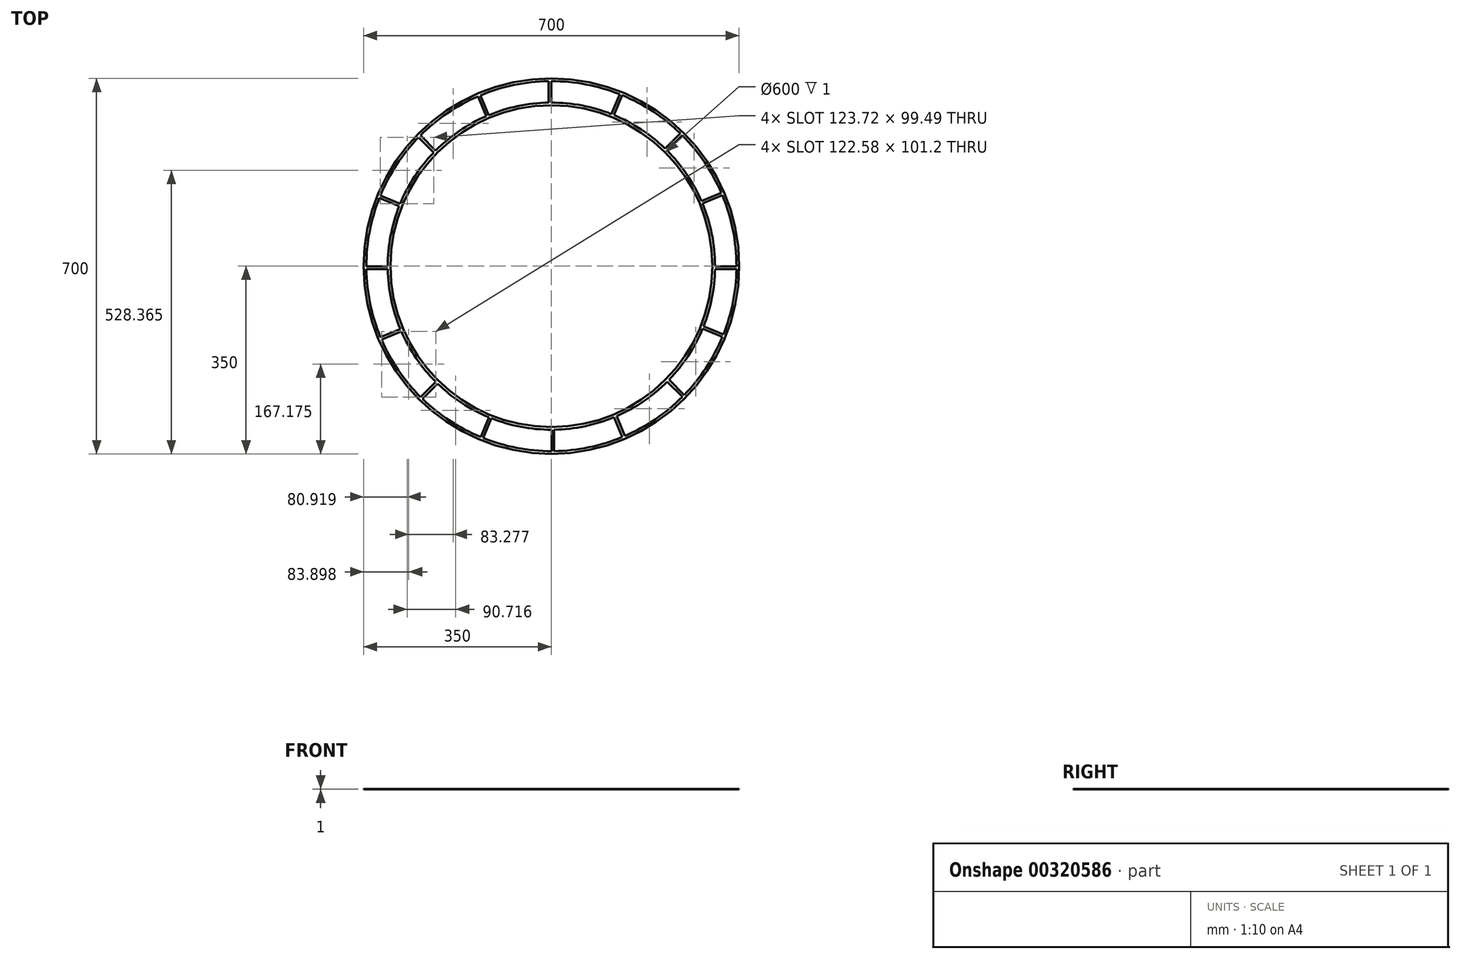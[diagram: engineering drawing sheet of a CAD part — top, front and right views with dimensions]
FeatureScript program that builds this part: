
annotation { "Feature Type Name" : "Feature", "Feature Type Description" : "" }
export const myFeature = defineFeature(function(context is Context, id is Id, definition is map)
    precondition{}
    {
        {
            var Q0;
            Q0=qCreatedBy(makeId("Top.planeOp"),FACE);
            var sketch = newSketch(context, id + "F0", { "sketchPlane" : qUnion([Q0])});
            skCircle(sketch, "E0", {"center": v(0, 0) * mm, "radius": 300 * mm});
            skArc(sketch, "E1", {"start": v(345, -0.2) * mm, "mid": v(338.37, 67.32) * mm, "end": v(318.65, 132.24) * mm});
            skCircle(sketch, "E2", {"center": v(0, 0) * mm, "radius": 350 * mm});
            skArc(sketch, "E3", {"start": v(305, -0.27) * mm, "mid": v(299.14, 59.48) * mm, "end": v(281.7, 116.93) * mm});
            skLineSegment(sketch, "E4", {"start": v(0, 0) * mm, "end": v(528.74, 0) * mm, "construction": true});
            skLineSegment(sketch, "E5.right", {"start": v(288.09, 5.23) * mm, "end": v(288.09, 0) * mm});
            skPoint(sketch, "E5.middle", {"position": v(324.27, 0) * mm});
            skLineSegment(sketch, "E6.1.0", {"start": v(331.02, 142.78) * mm, "end": v(321.32, 138.76) * mm});
            skLineSegment(sketch, "E6.1.1", {"start": v(332.97, 138.17) * mm, "end": v(323.27, 134.15) * mm});
            skLineSegment(sketch, "E6.2.0", {"start": v(251.18, 258.58) * mm, "end": v(243.76, 251.16) * mm});
            skLineSegment(sketch, "E6.2.1", {"start": v(254.75, 255.08) * mm, "end": v(247.32, 247.65) * mm});
            skLineSegment(sketch, "E6.3.0", {"start": v(133.1, 335.02) * mm, "end": v(129.1, 325.32) * mm});
            skLineSegment(sketch, "E6.3.1", {"start": v(137.74, 333.15) * mm, "end": v(133.73, 323.45) * mm});
            skLineSegment(sketch, "E6.4.1", {"start": v(-0.23, 360.5) * mm, "end": v(-0.23, 350) * mm});
            skLineSegment(sketch, "E6.5.0", {"start": v(-142.78, 331.02) * mm, "end": v(-138.76, 321.32) * mm});
            skLineSegment(sketch, "E6.5.1", {"start": v(-138.17, 332.97) * mm, "end": v(-134.15, 323.27) * mm});
            skLineSegment(sketch, "E6.6.0", {"start": v(-258.58, 251.18) * mm, "end": v(-251.16, 243.76) * mm});
            skLineSegment(sketch, "E6.6.1", {"start": v(-255.08, 254.75) * mm, "end": v(-247.65, 247.32) * mm});
            skLineSegment(sketch, "E6.7.0", {"start": v(-335.02, 133.1) * mm, "end": v(-283.74, 111.87) * mm});
            skLineSegment(sketch, "E6.7.1", {"start": v(-333.15, 137.74) * mm, "end": v(-281.87, 116.5) * mm});
            skLineSegment(sketch, "E6.8.0", {"start": v(-360.46, -5.23) * mm, "end": v(-349.96, -5.23) * mm});
            skLineSegment(sketch, "E6.8.1", {"start": v(-360.5, -0.23) * mm, "end": v(-350, -0.23) * mm});
            skLineSegment(sketch, "E6.9.0", {"start": v(-331.02, -142.78) * mm, "end": v(-321.32, -138.76) * mm});
            skLineSegment(sketch, "E6.9.1", {"start": v(-332.97, -138.17) * mm, "end": v(-323.27, -134.15) * mm});
            skLineSegment(sketch, "E6.10.0", {"start": v(-251.18, -258.58) * mm, "end": v(-243.76, -251.16) * mm});
            skLineSegment(sketch, "E6.10.1", {"start": v(-254.75, -255.08) * mm, "end": v(-247.32, -247.65) * mm});
            skLineSegment(sketch, "E6.11.0", {"start": v(-133.1, -335.02) * mm, "end": v(-129.1, -325.32) * mm});
            skLineSegment(sketch, "E6.11.1", {"start": v(-137.74, -333.15) * mm, "end": v(-133.73, -323.45) * mm});
            skLineSegment(sketch, "E6.12.0", {"start": v(5.23, -360.46) * mm, "end": v(5.23, -349.96) * mm});
            skLineSegment(sketch, "E6.12.1", {"start": v(0.23, -360.5) * mm, "end": v(0.23, -350) * mm});
            skLineSegment(sketch, "E6.13.0", {"start": v(142.78, -331.02) * mm, "end": v(138.76, -321.32) * mm});
            skLineSegment(sketch, "E6.13.1", {"start": v(138.17, -332.97) * mm, "end": v(134.15, -323.27) * mm});
            skLineSegment(sketch, "E6.14.0", {"start": v(258.58, -251.18) * mm, "end": v(251.16, -243.76) * mm});
            skLineSegment(sketch, "E6.14.1", {"start": v(255.08, -254.75) * mm, "end": v(247.65, -247.32) * mm});
            skLineSegment(sketch, "E6.15.0", {"start": v(335.02, -133.1) * mm, "end": v(325.32, -129.1) * mm});
            skLineSegment(sketch, "E6.15.1", {"start": v(333.15, -137.74) * mm, "end": v(323.45, -133.73) * mm});
            skPoint(sketch, "E7.orphan", {"position": v(288.09, -5.23) * mm});
            skLineSegment(sketch, "E8.trimOffspring", {"start": v(345, -0.2) * mm, "end": v(305, -0.27) * mm});
            skLineSegment(sketch, "E9.trimOffspring", {"start": v(344.96, -5.2) * mm, "end": v(304.95, -5.27) * mm});
            skPoint(sketch, "E5.left.start.orphan", {"position": v(360.46, 5.23) * mm});
            skPoint(sketch, "E5.top.start.orphan", {"position": v(360.46, -5.23) * mm});
            skArc(sketch, "E10.trimOffspring", {"start": v(316.7, 136.84) * mm, "mid": v(285.33, 193.94) * mm, "end": v(243.79, 244.12) * mm});
            skArc(sketch, "E11.trimOffspring", {"start": v(279.74, 121.53) * mm, "mid": v(252.07, 171.71) * mm, "end": v(215.5, 215.83) * mm});
            skArc(sketch, "E12.trimOffspring", {"start": v(211.94, 219.34) * mm, "mid": v(167.17, 255.1) * mm, "end": v(116.5, 281.87) * mm});
            skArc(sketch, "E13.trimOffspring", {"start": v(240.22, 247.62) * mm, "mid": v(189.4, 288.37) * mm, "end": v(131.81, 318.83) * mm});
            skArc(sketch, "E14.trimOffspring", {"start": v(127.18, 320.7) * mm, "mid": v(64.62, 338.9) * mm, "end": v(-0.23, 345) * mm});
            skArc(sketch, "E15.trimOffspring", {"start": v(111.87, 283.74) * mm, "mid": v(56.82, 299.66) * mm, "end": v(-0.23, 305) * mm});
            skArc(sketch, "E16.trimOffspring", {"start": v(-5.23, 344.96) * mm, "mid": v(-69.98, 337.83) * mm, "end": v(-132.24, 318.65) * mm});
            skArc(sketch, "E17.trimOffspring", {"start": v(-5.23, 304.96) * mm, "mid": v(-62.18, 298.6) * mm, "end": v(-116.93, 281.7) * mm});
            skArc(sketch, "E18.trimOffspring", {"start": v(-136.84, 316.7) * mm, "mid": v(-193.94, 285.33) * mm, "end": v(-244.12, 243.79) * mm});
            skArc(sketch, "E19.trimOffspring", {"start": v(-121.53, 279.74) * mm, "mid": v(-171.71, 252.07) * mm, "end": v(-215.83, 215.5) * mm});
            skArc(sketch, "E20.trimOffspring", {"start": v(-247.62, 240.22) * mm, "mid": v(-288.37, 189.4) * mm, "end": v(-318.83, 131.81) * mm});
            skArc(sketch, "E21.trimOffspring", {"start": v(-219.34, 211.94) * mm, "mid": v(-255.1, 167.17) * mm, "end": v(-281.87, 116.5) * mm});
            skArc(sketch, "E22.trimOffspring", {"start": v(-320.7, 127.18) * mm, "mid": v(-338.9, 64.62) * mm, "end": v(-345, -0.23) * mm});
            skArc(sketch, "E23.trimOffspring", {"start": v(-283.74, 111.87) * mm, "mid": v(-299.66, 56.82) * mm, "end": v(-305, -0.23) * mm});
            skArc(sketch, "E24.trimOffspring", {"start": v(-344.96, -5.23) * mm, "mid": v(-337.83, -69.98) * mm, "end": v(-318.65, -132.24) * mm});
            skArc(sketch, "E25.trimOffspring", {"start": v(-304.96, -5.23) * mm, "mid": v(-298.6, -62.18) * mm, "end": v(-281.7, -116.93) * mm});
            skArc(sketch, "E26.trimOffspring", {"start": v(-279.74, -121.53) * mm, "mid": v(-252.07, -171.71) * mm, "end": v(-215.5, -215.83) * mm});
            skArc(sketch, "E27.trimOffspring", {"start": v(-211.94, -219.34) * mm, "mid": v(-167.17, -255.1) * mm, "end": v(-116.5, -281.87) * mm});
            skArc(sketch, "E28.trimOffspring", {"start": v(-240.22, -247.62) * mm, "mid": v(-189.4, -288.37) * mm, "end": v(-131.81, -318.83) * mm});
            skArc(sketch, "E29.trimOffspring", {"start": v(-111.87, -283.74) * mm, "mid": v(-56.82, -299.66) * mm, "end": v(0.23, -305) * mm});
            skArc(sketch, "E30.trimOffspring", {"start": v(-127.18, -320.7) * mm, "mid": v(-64.62, -338.9) * mm, "end": v(0.23, -345) * mm});
            skArc(sketch, "E31.trimOffspring", {"start": v(5.23, -304.96) * mm, "mid": v(62.18, -298.6) * mm, "end": v(116.93, -281.7) * mm});
            skArc(sketch, "E32.trimOffspring", {"start": v(5.23, -344.96) * mm, "mid": v(69.98, -337.83) * mm, "end": v(132.24, -318.65) * mm});
            skArc(sketch, "E33.trimOffspring", {"start": v(136.84, -316.7) * mm, "mid": v(193.94, -285.33) * mm, "end": v(244.12, -243.79) * mm});
            skArc(sketch, "E34.trimOffspring", {"start": v(121.53, -279.74) * mm, "mid": v(171.71, -252.07) * mm, "end": v(215.83, -215.5) * mm});
            skArc(sketch, "E35.trimOffspring", {"start": v(219.34, -211.94) * mm, "mid": v(255.1, -167.17) * mm, "end": v(281.87, -116.5) * mm});
            skArc(sketch, "E36.trimOffspring", {"start": v(247.62, -240.22) * mm, "mid": v(288.37, -189.4) * mm, "end": v(318.83, -131.81) * mm});
            skArc(sketch, "E37.trimOffspring", {"start": v(283.74, -111.87) * mm, "mid": v(299.14, -59.52) * mm, "end": v(304.95, -5.27) * mm});
            skArc(sketch, "E38.trimOffspring", {"start": v(320.7, -127.18) * mm, "mid": v(338.37, -67.29) * mm, "end": v(344.96, -5.2) * mm});
            skLineSegment(sketch, "E39.trimOffspring", {"start": v(275.12, 119.62) * mm, "end": v(264.16, 115.08) * mm});
            skLineSegment(sketch, "E40.trimOffspring", {"start": v(277.08, 115.02) * mm, "end": v(266.11, 110.48) * mm});
            skLineSegment(sketch, "E41.trimOffspring", {"start": v(316.7, 136.84) * mm, "end": v(279.74, 121.53) * mm});
            skLineSegment(sketch, "E42.trimOffspring", {"start": v(318.65, 132.24) * mm, "end": v(281.7, 116.93) * mm});
            skLineSegment(sketch, "E43.trimOffspring", {"start": v(240.22, 247.62) * mm, "end": v(211.94, 219.34) * mm});
            skLineSegment(sketch, "E44.trimOffspring", {"start": v(243.79, 244.12) * mm, "end": v(215.5, 215.83) * mm});
            skLineSegment(sketch, "E45.trimOffspring", {"start": v(211.97, 212.3) * mm, "end": v(203.58, 203.9) * mm});
            skLineSegment(sketch, "E46.trimOffspring", {"start": v(208.4, 215.8) * mm, "end": v(200.01, 207.4) * mm});
            skLineSegment(sketch, "E47.trimOffspring", {"start": v(127.18, 320.7) * mm, "end": v(111.87, 283.74) * mm});
            skLineSegment(sketch, "E48.trimOffspring", {"start": v(131.81, 318.83) * mm, "end": v(116.5, 281.87) * mm});
            skLineSegment(sketch, "E49.trimOffspring", {"start": v(109.95, 279.12) * mm, "end": v(105.41, 268.16) * mm});
            skLineSegment(sketch, "E50.trimOffspring", {"start": v(114.6, 277.25) * mm, "end": v(110.05, 266.29) * mm});
            skLineSegment(sketch, "E51.trimOffspring", {"start": v(-0.23, 345) * mm, "end": v(-0.23, 305) * mm});
            skLineSegment(sketch, "E52.trimOffspring", {"start": v(-5.23, 344.96) * mm, "end": v(-5.23, 304.96) * mm});
            skLineSegment(sketch, "E53.trimOffspring", {"start": v(-0.23, 300) * mm, "end": v(-0.23, 288.13) * mm});
            skLineSegment(sketch, "E54.trimOffspring", {"start": v(-5.23, 299.95) * mm, "end": v(-5.23, 288.09) * mm});
            skLineSegment(sketch, "E55.trimOffspring", {"start": v(-132.24, 318.65) * mm, "end": v(-116.93, 281.7) * mm});
            skLineSegment(sketch, "E56.trimOffspring", {"start": v(-136.84, 316.7) * mm, "end": v(-121.53, 279.74) * mm});
            skLineSegment(sketch, "E57.trimOffspring", {"start": v(-115.02, 277.08) * mm, "end": v(-110.48, 266.11) * mm});
            skLineSegment(sketch, "E58.trimOffspring", {"start": v(-119.62, 275.12) * mm, "end": v(-115.08, 264.16) * mm});
            skLineSegment(sketch, "E59.trimOffspring", {"start": v(-244.12, 243.79) * mm, "end": v(-215.83, 215.5) * mm});
            skLineSegment(sketch, "E60.trimOffspring", {"start": v(-247.62, 240.22) * mm, "end": v(-219.34, 211.94) * mm});
            skLineSegment(sketch, "E61.trimOffspring", {"start": v(-212.3, 211.97) * mm, "end": v(-203.9, 203.58) * mm});
            skLineSegment(sketch, "E62.trimOffspring", {"start": v(-215.8, 208.4) * mm, "end": v(-207.4, 200.01) * mm});
            skLineSegment(sketch, "E63.trimOffspring", {"start": v(-277.25, 114.6) * mm, "end": v(-266.29, 110.05) * mm});
            skLineSegment(sketch, "E64.trimOffspring", {"start": v(-279.12, 109.95) * mm, "end": v(-268.16, 105.41) * mm});
            skLineSegment(sketch, "E65.trimOffspring", {"start": v(-300, -0.23) * mm, "end": v(-288.13, -0.23) * mm});
            skLineSegment(sketch, "E66.trimOffspring", {"start": v(-299.95, -5.23) * mm, "end": v(-288.09, -5.23) * mm});
            skLineSegment(sketch, "E67.trimOffspring", {"start": v(-344.96, -5.23) * mm, "end": v(-304.96, -5.23) * mm});
            skLineSegment(sketch, "E68.trimOffspring", {"start": v(-345, -0.23) * mm, "end": v(-305, -0.23) * mm});
            skLineSegment(sketch, "E69.trimOffspring", {"start": v(-277.08, -115.02) * mm, "end": v(-266.11, -110.48) * mm});
            skLineSegment(sketch, "E70.trimOffspring", {"start": v(-275.12, -119.62) * mm, "end": v(-264.16, -115.08) * mm});
            skLineSegment(sketch, "E71.trimOffspring", {"start": v(-316.7, -136.84) * mm, "end": v(-279.74, -121.53) * mm});
            skLineSegment(sketch, "E72.trimOffspring", {"start": v(-318.65, -132.24) * mm, "end": v(-281.7, -116.93) * mm});
            skArc(sketch, "E73.trimOffspring", {"start": v(-316.7, -136.84) * mm, "mid": v(-285.33, -193.94) * mm, "end": v(-243.79, -244.12) * mm});
            skLineSegment(sketch, "E74.trimOffspring", {"start": v(-243.79, -244.12) * mm, "end": v(-215.5, -215.83) * mm});
            skLineSegment(sketch, "E75.trimOffspring", {"start": v(-240.22, -247.62) * mm, "end": v(-211.94, -219.34) * mm});
            skLineSegment(sketch, "E76.trimOffspring", {"start": v(-211.97, -212.3) * mm, "end": v(-203.58, -203.9) * mm});
            skLineSegment(sketch, "E77.trimOffspring", {"start": v(-208.4, -215.8) * mm, "end": v(-200.01, -207.4) * mm});
            skLineSegment(sketch, "E78.trimOffspring", {"start": v(-114.6, -277.25) * mm, "end": v(-110.05, -266.29) * mm});
            skLineSegment(sketch, "E79.trimOffspring", {"start": v(-131.81, -318.83) * mm, "end": v(-116.5, -281.87) * mm});
            skLineSegment(sketch, "E80.trimOffspring", {"start": v(-127.18, -320.7) * mm, "end": v(-111.87, -283.74) * mm});
            skLineSegment(sketch, "E81.trimOffspring", {"start": v(-109.95, -279.12) * mm, "end": v(-105.41, -268.16) * mm});
            skLineSegment(sketch, "E82.trimOffspring", {"start": v(0.23, -300) * mm, "end": v(0.23, -288.13) * mm});
            skLineSegment(sketch, "E83.trimOffspring", {"start": v(5.23, -299.95) * mm, "end": v(5.23, -288.09) * mm});
            skLineSegment(sketch, "E84.trimOffspring", {"start": v(0.23, -345) * mm, "end": v(0.23, -305) * mm});
            skLineSegment(sketch, "E85.trimOffspring", {"start": v(5.23, -344.96) * mm, "end": v(5.23, -304.96) * mm});
            skLineSegment(sketch, "E86.trimOffspring", {"start": v(115.02, -277.08) * mm, "end": v(110.48, -266.11) * mm});
            skLineSegment(sketch, "E87.trimOffspring", {"start": v(119.62, -275.12) * mm, "end": v(115.08, -264.16) * mm});
            skLineSegment(sketch, "E88.trimOffspring", {"start": v(136.84, -316.7) * mm, "end": v(121.53, -279.74) * mm});
            skLineSegment(sketch, "E89.trimOffspring", {"start": v(132.24, -318.65) * mm, "end": v(116.93, -281.7) * mm});
            skLineSegment(sketch, "E90.trimOffspring", {"start": v(212.3, -211.97) * mm, "end": v(203.9, -203.58) * mm});
            skLineSegment(sketch, "E91.trimOffspring", {"start": v(215.8, -208.4) * mm, "end": v(207.4, -200.01) * mm});
            skLineSegment(sketch, "E92.trimOffspring", {"start": v(247.62, -240.22) * mm, "end": v(219.34, -211.94) * mm});
            skLineSegment(sketch, "E93.trimOffspring", {"start": v(244.12, -243.79) * mm, "end": v(215.83, -215.5) * mm});
            skLineSegment(sketch, "E94.trimOffspring", {"start": v(279.12, -109.95) * mm, "end": v(268.16, -105.41) * mm});
            skLineSegment(sketch, "E95.trimOffspring", {"start": v(277.25, -114.6) * mm, "end": v(266.29, -110.05) * mm});
            skLineSegment(sketch, "E96.trimOffspring", {"start": v(318.83, -131.81) * mm, "end": v(281.87, -116.5) * mm});
            skLineSegment(sketch, "E97.trimOffspring", {"start": v(320.7, -127.18) * mm, "end": v(283.74, -111.87) * mm});
            skSolve(sketch);
        }
        {
            var Q0;
            Q0=makeQuery(id+"F0.imprint","IMPRINT",FACE,{"disambiguationData":[TD([[makeQuery(id+"F0.imprint","IMPRINT",EDGE,{"derivedFrom":sQuery(id+"F0.wireOp",EDGE,"E1")}),-1.0]])]});
            extrude(context, id + "F1", {"entities" : qUnion([Q0]), "depth" : 1 * mm});
        }
    });
